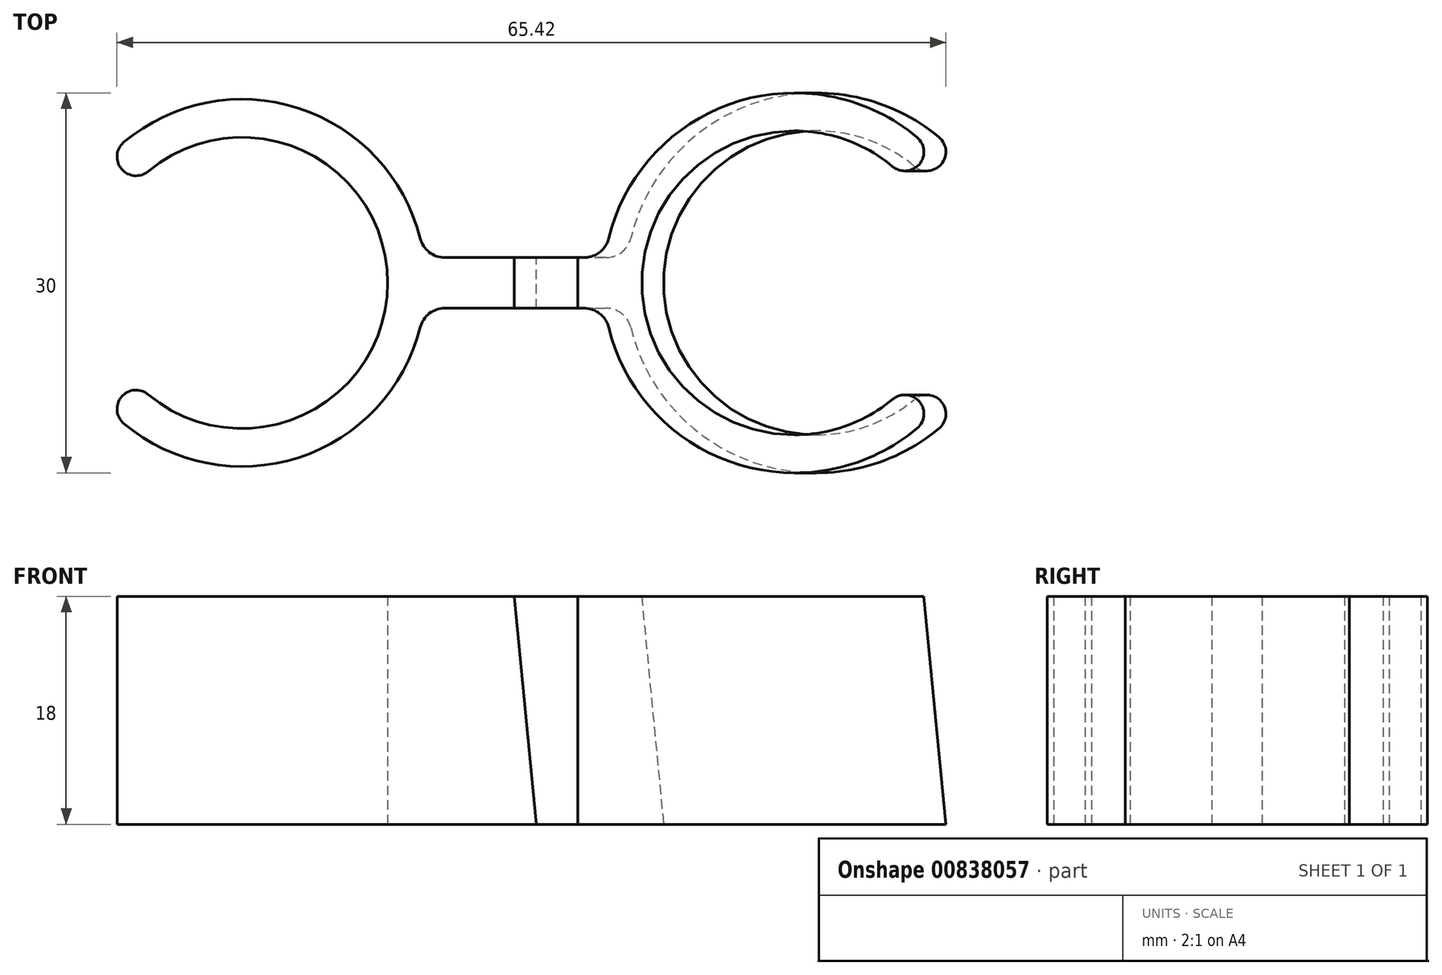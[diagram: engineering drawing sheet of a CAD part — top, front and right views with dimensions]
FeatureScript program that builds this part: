
annotation { "Feature Type Name" : "Feature", "Feature Type Description" : "" }
export const myFeature = defineFeature(function(context is Context, id is Id, definition is map)
    precondition{}
    {
        {
            assignVariable(context, id + "F0", {"name" : "Kulma", "anyValue" : 5.5});
        }
        {
            var Q0;
            Q0=qCreatedBy(makeId("Top.planeOp"),FACE);
            var sketch = newSketch(context, id + "F1", { "sketchPlane" : qUnion([Q0])});
            skArc(sketch, "E0", {"start": v(-7.4, -8.8) * mm, "mid": v(11.5, 0) * mm, "end": v(-7.4, 8.8) * mm});
            skArc(sketch, "E1", {"start": v(-9.32, -11.1) * mm, "mid": v(14.5, 0) * mm, "end": v(-9.32, 11.1) * mm});
            skLineSegment(sketch, "E2", {"start": v(0, 0) * mm, "end": v(-19.82, 23.62) * mm, "construction": true});
            skLineSegment(sketch, "E3.MirrorCS", {"start": v(0, 0) * mm, "end": v(-19.82, -23.62) * mm, "construction": true});
            skArc(sketch, "E4", {"start": v(-9.32, 11.1) * mm, "mid": v(-9.5, 9) * mm, "end": v(-7.4, 8.8) * mm});
            skArc(sketch, "E5", {"start": v(-7.4, -8.8) * mm, "mid": v(-9.5, -9) * mm, "end": v(-9.32, -11.1) * mm});
            skLineSegment(sketch, "E6", {"start": v(14.36, 2) * mm, "end": v(26.5, 2) * mm});
            skLineSegment(sketch, "E7.MirrorCS", {"start": v(14.36, -2) * mm, "end": v(26.5, -2) * mm});
            skLineSegment(sketch, "E8", {"start": v(26.5, 2) * mm, "end": v(26.5, -2) * mm});
            skPoint(sketch, "E9", {"position": v(11.5, 0) * mm});
            skSolve(sketch);
        }
        {
            var Q0;
            Q0=makeQuery(id+"F1.imprint","IMPRINT",FACE,{"disambiguationData":[TD([[makeQuery(id+"F1.imprint","IMPRINT",EDGE,{"derivedFrom":sQuery(id+"F1.wireOp",EDGE,"E0")}),-1.0]])]});
            var Q1;
            {var subQ0=sQuery(id+"F1.wireOp",EDGE,"E6");Q1=makeQuery(id+"F1.imprint","IMPRINT",FACE,{"disambiguationData":[TD([[makeQuery(id+"F1.imprint","IMPRINT",EDGE,{"derivedFrom":subQ0}),-1.0]])]});}
            extrude(context, id + "F2", {"entities" : qUnion([Q0, Q1]), "depth" : 25 * mm, "offsetDistance" : 25 * mm});
        }
        {
            var Q0;
            Q0=makeQuery(id+"F2.opExtrude","CAP_FACE",FACE,{"disambiguationData":[OSD([sQuery(id+"F1.wireOp",EDGE,"E0"),sQuery(id+"F1.wireOp",EDGE,"E1"),sQuery(id+"F1.wireOp",EDGE,"E4"),sQuery(id+"F1.wireOp",EDGE,"E5"),sQuery(id+"F1.wireOp",EDGE,"E6"),sQuery(id+"F1.wireOp",EDGE,"E7.MirrorCS"),sQuery(id+"F1.wireOp",EDGE,"E8")])],"isStart":true});
            var sketch = newSketch(context, id + "F3", { "sketchPlane" : qUnion([Q0])});
            skArc(sketch, "E10", {"start": v(51.21, 9.2) * mm, "mid": v(31.5, 0) * mm, "end": v(51.21, -9.2) * mm});
            skArc(sketch, "E11", {"start": v(53.14, 11.5) * mm, "mid": v(28.5, 0) * mm, "end": v(53.14, -11.5) * mm});
            skLineSegment(sketch, "E12", {"start": v(43.5, 0) * mm, "end": v(56.79, 15.84) * mm, "construction": true});
            skLineSegment(sketch, "E13.MirrorCS", {"start": v(43.5, 0) * mm, "end": v(56.79, -15.84) * mm, "construction": true});
            skArc(sketch, "E14", {"start": v(51.21, 9.2) * mm, "mid": v(53.33, 9.38) * mm, "end": v(53.14, 11.5) * mm});
            skArc(sketch, "E15", {"start": v(53.14, -11.5) * mm, "mid": v(53.33, -9.38) * mm, "end": v(51.21, -9.2) * mm});
            skLineSegment(sketch, "E16", {"start": v(28.63, 2) * mm, "end": v(21.5, 2) * mm});
            skLineSegment(sketch, "E17.MirrorCS", {"start": v(28.63, -2) * mm, "end": v(21.5, -2) * mm});
            skLineSegment(sketch, "E18", {"start": v(21.5, 2) * mm, "end": v(21.5, -2) * mm});
            skPoint(sketch, "E19", {"position": v(31.5, 0) * mm});
            skPoint(sketch, "E20", {"position": v(11.5, 0) * mm});
            skSolve(sketch);
        }
        {
            var Q0;
            Q0=makeQuery(id+"F3.imprint","IMPRINT",FACE,{"disambiguationData":[TD([[makeQuery(id+"F3.imprint","IMPRINT",EDGE,{"derivedFrom":sQuery(id+"F3.wireOp",EDGE,"E10")}),-1.0]])]});
            var Q1;
            {var subQ2=sQuery(id+"F3.wireOp",EDGE,"E18");Q1=makeQuery(id+"F3.imprint","IMPRINT",FACE,{"disambiguationData":[TD([[makeQuery(id+"F3.imprint","IMPRINT",EDGE,{"derivedFrom":subQ2}),1.0]])]});}
            var Q2;
            {var subQ5=makeQuery(id+"F2.opExtrude","CAP_EDGE",EDGE,{"disambiguationData":[OSD([sQuery(id+"F1.wireOp",EDGE,"E8")])],"isStart":true});Q2=makeQuery(id+"F3.imprint","IMPRINT",FACE,{"disambiguationData":[TD([[makeQuery(id+"F3.imprint","IMPRINT",EDGE,{"derivedFrom":subQ5}),-1.0]])]});}
            extrude(context, id + "F4", {"entities" : qUnion([Q0, Q1, Q2]), "oppositeDirection" : true, "depth" : 25 * mm, "offsetDistance" : 25 * mm});
        }
        {
            var Q0;
            Q0=makeQuery(id+"F4.opExtrude","SWEPT_BODY",BODY,{"disambiguationData":[OSD([sQuery(id+"F3.wireOp",EDGE,"E10"),sQuery(id+"F3.wireOp",EDGE,"E11"),sQuery(id+"F3.wireOp",EDGE,"E14"),sQuery(id+"F3.wireOp",EDGE,"E15"),sQuery(id+"F3.wireOp",EDGE,"E16"),sQuery(id+"F3.wireOp",EDGE,"E17.MirrorCS"),sQuery(id+"F3.wireOp",EDGE,"E18")])]});
            var Q1;
            Q1=makeQuery(id+"F4.opExtrude","CAP_EDGE",EDGE,{"disambiguationData":[OSD([sQuery(id+"F3.wireOp",EDGE,"E18")])],"isStart":false});
            transform(context, id + "F5", {"entities" : qUnion([Q0]), "transformType" : TransformType.ROTATION, "transformAxis" : qUnion([Q1]), "angle" : (getVariable(context, 'Kulma')) * degree, "oppositeDirection" : true, "makeCopy" : false});
        }
        {
            var Q0;
            Q0=qCreatedBy(makeId("Top.planeOp"),FACE);
            var sketch = newSketch(context, id + "F6", { "sketchPlane" : qUnion([Q0])});
            skLineSegment(sketch, "E21.bottom", {"start": v(-24.69, 25.86) * mm, "end": v(79.54, 25.86) * mm});
            skLineSegment(sketch, "E21.top", {"start": v(-24.69, -31.35) * mm, "end": v(79.54, -31.35) * mm});
            skLineSegment(sketch, "E21.left", {"start": v(-24.69, 25.86) * mm, "end": v(-24.69, -31.35) * mm});
            skLineSegment(sketch, "E21.right", {"start": v(79.54, 25.86) * mm, "end": v(79.54, -31.35) * mm});
            skSolve(sketch);
        }
        {
            var Q0;
            Q0=makeQuery(id+"F6.imprint","IMPRINT",FACE,{"disambiguationData":[TD([[makeQuery(id+"F6.imprint","IMPRINT",EDGE,{"derivedFrom":sQuery(id+"F6.wireOp",EDGE,"E21.bottom")}),-1.0]])]});
            extrude(context, id + "F7", {"entities" : qUnion([Q0]), "operationType" : NewBodyOperationType.REMOVE, "endBound" : BoundingType.SYMMETRIC, "depth" : 14 * mm, "offsetDistance" : 25 * mm});
        }
        {
            var Q0;
            Q0=makeQuery(id+"F2.opExtrude","CAP_FACE",FACE,{"disambiguationData":[OSD([sQuery(id+"F1.wireOp",EDGE,"E0"),sQuery(id+"F1.wireOp",EDGE,"E1"),sQuery(id+"F1.wireOp",EDGE,"E4"),sQuery(id+"F1.wireOp",EDGE,"E5"),sQuery(id+"F1.wireOp",EDGE,"E6"),sQuery(id+"F1.wireOp",EDGE,"E7.MirrorCS"),sQuery(id+"F1.wireOp",EDGE,"E8")])],"isStart":false});
            var sketch = newSketch(context, id + "F8", { "sketchPlane" : qUnion([Q0])});
            skLineSegment(sketch, "E22.bottom", {"start": v(-23.95, 21.06) * mm, "end": v(76.9, 21.06) * mm});
            skLineSegment(sketch, "E22.top", {"start": v(-23.95, -25.12) * mm, "end": v(76.9, -25.12) * mm});
            skLineSegment(sketch, "E22.left", {"start": v(-23.95, 21.06) * mm, "end": v(-23.95, -25.12) * mm});
            skLineSegment(sketch, "E22.right", {"start": v(76.9, 21.06) * mm, "end": v(76.9, -25.12) * mm});
            skSolve(sketch);
        }
        {
            var Q0;
            Q0 = qSketchRegion(id + "F8", true);
            extrude(context, id + "F9", {"entities" : qUnion([Q0]), "operationType" : NewBodyOperationType.REMOVE, "depth" : 25 * mm, "offsetDistance" : 25 * mm});
        }
        {
            var Q0;
            Q0=makeQuery(id+"F2.opExtrude","SWEPT_EDGE",EDGE,{"disambiguationData":[OSD([sQuery(id+"F1.wireOp",EDGE,"E1"),sQuery(id+"F1.wireOp",EDGE,"E7.MirrorCS")])]});
            var Q1;
            Q1=makeQuery(id+"F4.opExtrude","SWEPT_EDGE",EDGE,{"disambiguationData":[OSD([sQuery(id+"F3.wireOp",EDGE,"E11"),sQuery(id+"F3.wireOp",EDGE,"E16")])]});
            var Q2;
            Q2=makeQuery(id+"F2.opExtrude","SWEPT_EDGE",EDGE,{"disambiguationData":[OSD([sQuery(id+"F1.wireOp",EDGE,"E1"),sQuery(id+"F1.wireOp",EDGE,"E6")])]});
            var Q3;
            Q3=makeQuery(id+"F4.opExtrude","SWEPT_EDGE",EDGE,{"disambiguationData":[OSD([sQuery(id+"F3.wireOp",EDGE,"E11"),sQuery(id+"F3.wireOp",EDGE,"E17.MirrorCS")])]});
            fillet(context, id + "F10", {"entities" : qUnion([Q0, Q1, Q2, Q3]), "radius" : 2 * mm, "tangentPropagation" : true, "allowEdgeOverflow" : false});
        }
    });
